# Revit family: Building-ConnessioniIEC309-GEWISS-66IB-PRESE-INTERBLOCCATE-HD_IP66_CON_FONDO_FUS
name_source: partatom
category: Apparecchi elettrici
units: mm (PartAtom-declared; Revit-internal decimal feet)

## family parameters
Condiviso = Sì
Host = Superficie
Mantenere orientamento annotazione = Sì
Punto di calcolo locali = Sì
Quota connettore circolare = Usa diametro
Taglio con vuoti quando caricato = Sì
Tipo di parte = Normale

## types (1)
- Building-ConnessioniIEC309-GEWISS-66IB-PRESE-INTERBLOCCATE-HD_IP66_CON_FONDO_FUS
    Catalogo = BUILDING
    Catalogo Serie = 66 IB
    Codice EAN = 8011564074446
    Codice Electrocod = 2222
    Colore = Rosso
    Colore: = Rosso
    Con fondo = Si
    Corpo presa = Light Blue
    Corrente nominale (A) = 32
    Corrente nominale (In) = 32
    Descrizione = PRESA BL.IP66 C.F.3P+T 32A 380V 3H CBF
    Frequenza = 50/60 Hz
    Frequenza nominale (Hz) = 50/60 Hz
    Glow Wire Test = 850 °C
    Glow wire test: = 850 °C
    Grado di protezione = IP66
    IDF = b00cc055-93cd-40b8-8f21-2b850c09e6a3
    IDT = 59f79668-9a62-484f-b845-13f84bd98f98
    Immagine tipo = S.jpg
    Modello = GW66973
    N. poli = 3P+T
    N_poli = 1
    Numero di poli = 3P+T
    Produttore = GEWISS S.p.A.
    Prospetto di default = 1219 mm
    Protezione = Base portafusibile (CBF)
    Resistenza agli urti = > IK10
    Resistenza agli urti a -20°C = 20J
    Riferimento h = 3
    SEO = Presa
    Scheda Tecnica = https://www.gewiss.com
    Simbolo presa = PRESAINDSTAGNA : 3P
    Struttura = Grigio RAL - 7035
    Temperatura di funzionamento = -25 ÷ +40 °C
    Temperatura di utilizzo = -25 +40 °C
    Tensione nominale = 380-440V
    Termopressione con biglia = 80 °C
    Tipo di impiego = Impieghi gravosi
    Tipo fusibile = Ø 10,3x38 mm
    Tipologia = Verticale
    URL = https://www.gewiss.com
    Versione file RFA = 21.4
    giallo = 0 mm  [stored 0 ft]
    presa = Grigio RAL - 7035
    vetro = Default - Vetro
    voltaggio = 0 V

note: [stored X ft] marks values corroborated as IEEE doubles in the binary element streams (Revit-internal decimal feet)

## geometry (parser evidence)
native form markers: Sweep x6
no freeform markers — native parametric forms only
